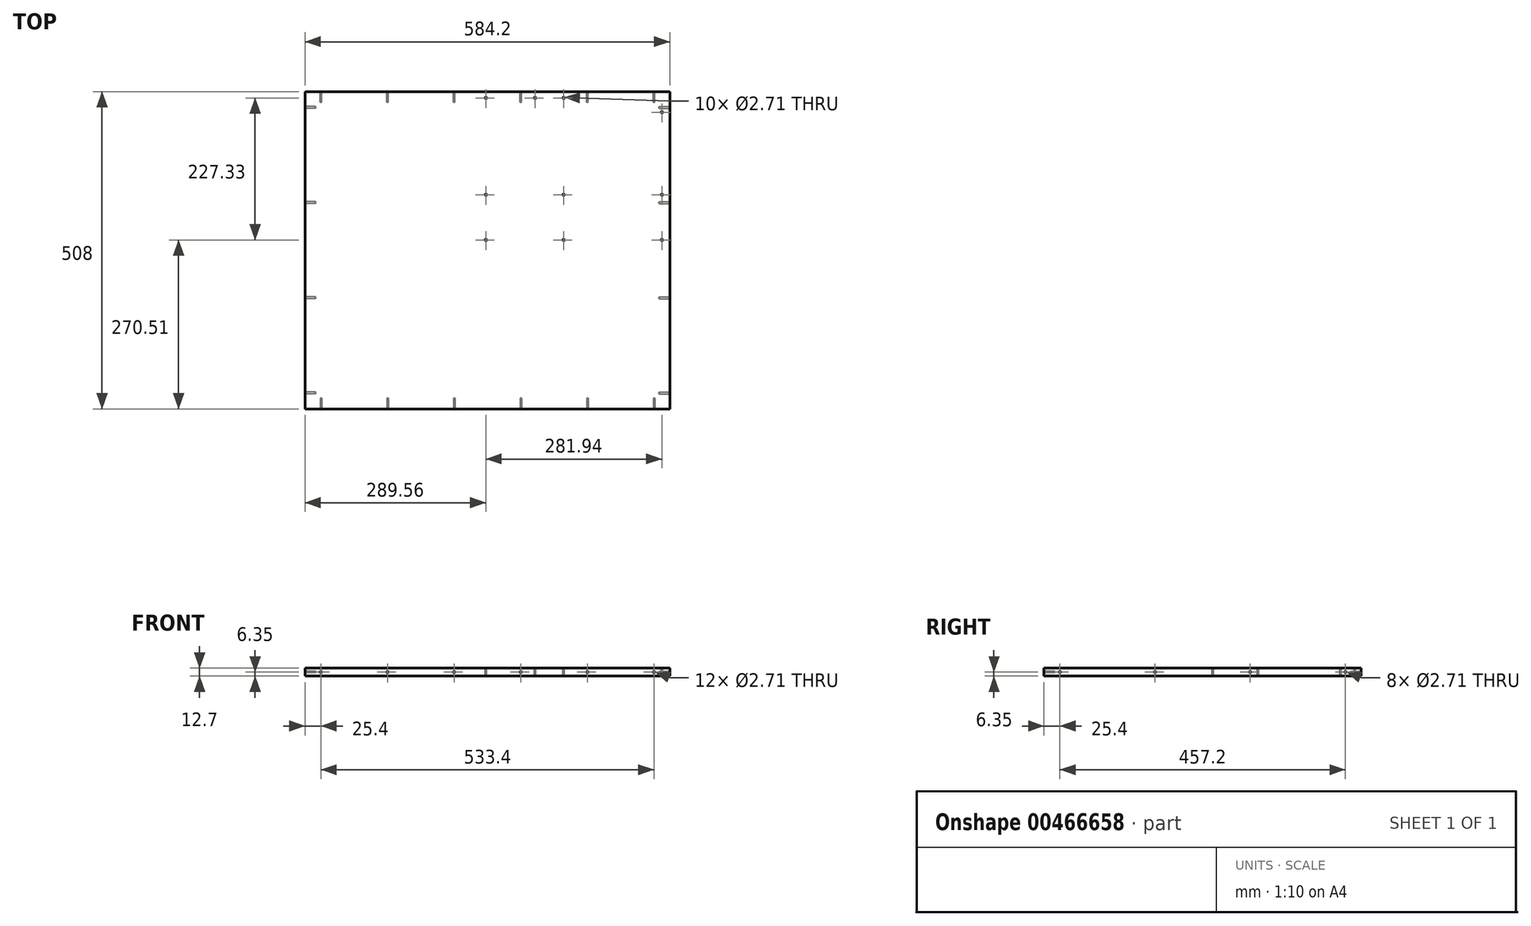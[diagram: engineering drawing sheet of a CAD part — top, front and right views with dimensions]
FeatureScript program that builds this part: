
annotation { "Feature Type Name" : "Feature", "Feature Type Description" : "" }
export const myFeature = defineFeature(function(context is Context, id is Id, definition is map)
    precondition{}
    {
        {
            var Q0;
            Q0=qCreatedBy(makeId("Top.planeOp"),FACE);
            var sketch = newSketch(context, id + "F0", { "sketchPlane" : qUnion([Q0])});
            skLineSegment(sketch, "E0.bottom", {"start": v(0, 0) * mm, "end": v(-584.2, 0) * mm});
            skLineSegment(sketch, "E0.top", {"start": v(0, -508) * mm, "end": v(-584.2, -508) * mm});
            skLineSegment(sketch, "E0.left", {"start": v(0, 0) * mm, "end": v(0, -508) * mm});
            skLineSegment(sketch, "E0.right", {"start": v(-584.2, 0) * mm, "end": v(-584.2, -508) * mm});
            skSolve(sketch);
        }
        {
            var Q0;
            Q0 = qSketchRegion(id + "F0", true);
            extrude(context, id + "F1", {"entities" : qUnion([Q0]), "depth" : 12.7 * mm});
        }
        {
            var Q0;
            Q0=makeQuery(id+"F1.opExtrude","SWEPT_FACE",FACE,{"disambiguationData":[OSD([sQuery(id+"F0.wireOp",EDGE,"E0.left")])]});
            var sketch = newSketch(context, id + "F2", { "sketchPlane" : qUnion([Q0])});
            skPoint(sketch, "E1", {"position": v(-25.4, 6.35) * mm});
            skPoint(sketch, "E2", {"position": v(-722.68, 6.35) * mm});
            skPoint(sketch, "E3", {"position": v(-330.2, 6.35) * mm});
            skPoint(sketch, "E4", {"position": v(-177.8, 6.35) * mm});
            skPoint(sketch, "E5", {"position": v(-482.6, 6.35) * mm});
            skSolve(sketch);
        }
        {
            var Q0;
            Q0=sQuery(id+"F2.wireOp",VERTEX,"E1");
            var Q1;
            Q1=sQuery(id+"F2.wireOp",VERTEX,"E4");
            var Q2;
            Q2=sQuery(id+"F2.wireOp",VERTEX,"E3");
            var Q3;
            Q3=sQuery(id+"F2.wireOp",VERTEX,"E2");
            var Q4;
            Q4=sQuery(id+"F2.wireOp",VERTEX,"E5");
            var Q5;
            Q5=makeQuery(id+"F1.opExtrude","SWEPT_BODY",BODY,{"disambiguationData":[OSD([sQuery(id+"F0.wireOp",EDGE,"E0.bottom"),sQuery(id+"F0.wireOp",EDGE,"E0.top"),sQuery(id+"F0.wireOp",EDGE,"E0.left"),sQuery(id+"F0.wireOp",EDGE,"E0.right")])]});
            hole(context, id + "F3", {"style" : HoleStyle.SIMPLE, "endStyle" : HoleEndStyle.BLIND, "standardTappedOrClearance" : lookupTablePath({ "standard" : "ANSI", "engagement" : "75%", "pitch" : "32 tpi", "size" : "#6", "type" : "Tapped" }), "standardBlindInLast" : lookupTablePath({ "standard" : "ANSI", "engagement" : "75%", "pitch" : "32 tpi", "size" : "#6", "type" : "Tapped" }), "holeDiameter" : 2.7 * mm, "showTappedDepth" : true, "holeDepth" : 16.67 * mm, "isTappedThrough" : true, "tappedDepth" : 12.7 * mm, "tapClearance" : 5, "locations" : qUnion([Q0, Q1, Q2, Q3, Q4]), "scope" : qUnion([Q5]), "majorDiameter" : 3.5 * mm});
        }
        {
            var Q0;
            Q0=makeQuery(id+"F1.opExtrude","SWEPT_FACE",FACE,{"disambiguationData":[OSD([sQuery(id+"F0.wireOp",EDGE,"E0.top")])]});
            var sketch = newSketch(context, id + "F4", { "sketchPlane" : qUnion([Q0])});
            skPoint(sketch, "E6", {"position": v(-25.4, 6.35) * mm});
            skPoint(sketch, "E7.1.0.0", {"position": v(-132.08, 6.35) * mm});
            skPoint(sketch, "E7.2.0.0", {"position": v(-238.76, 6.35) * mm});
            skPoint(sketch, "E7.3.0.0", {"position": v(-345.44, 6.35) * mm});
            skPoint(sketch, "E7.4.0.0", {"position": v(-452.12, 6.35) * mm});
            skLineSegment(sketch, "E7.direction1", {"start": v(-25.4, 6.35) * mm, "end": v(-132.08, 6.35) * mm, "construction": true});
            skPoint(sketch, "E8.0.5.0", {"position": v(-558.8, 6.35) * mm});
            skSolve(sketch);
        }
        {
            var Q0;
            Q0=sQuery(id+"F4.wireOp",VERTEX,"E6");
            var Q1;
            Q1=sQuery(id+"F4.wireOp",VERTEX,"E7.1.0.0");
            var Q2;
            Q2=sQuery(id+"F4.wireOp",VERTEX,"E7.2.0.0");
            var Q3;
            Q3=sQuery(id+"F4.wireOp",VERTEX,"E7.3.0.0");
            var Q4;
            Q4=sQuery(id+"F4.wireOp",VERTEX,"E7.4.0.0");
            var Q5;
            Q5=sQuery(id+"F4.wireOp",VERTEX,"E8.0.5.0");
            var Q6;
            Q6=makeQuery(id+"F1.opExtrude","SWEPT_BODY",BODY,{"disambiguationData":[OSD([sQuery(id+"F0.wireOp",EDGE,"E0.bottom"),sQuery(id+"F0.wireOp",EDGE,"E0.top"),sQuery(id+"F0.wireOp",EDGE,"E0.left"),sQuery(id+"F0.wireOp",EDGE,"E0.right")])]});
            hole(context, id + "F5", {"style" : HoleStyle.SIMPLE, "endStyle" : HoleEndStyle.BLIND, "standardTappedOrClearance" : lookupTablePath({ "standard" : "ANSI", "engagement" : "75%", "pitch" : "32 tpi", "size" : "#6", "type" : "Tapped" }), "standardBlindInLast" : lookupTablePath({ "standard" : "ANSI", "engagement" : "75%", "pitch" : "32 tpi", "size" : "#6", "type" : "Tapped" }), "holeDiameter" : 2.7 * mm, "showTappedDepth" : true, "holeDepth" : 16.66 * mm, "isTappedThrough" : true, "tappedDepth" : 12.7 * mm, "tapClearance" : 5, "locations" : qUnion([Q0, Q1, Q2, Q3, Q4, Q5]), "scope" : qUnion([Q6]), "majorDiameter" : 3.5 * mm});
        }
        {
            var Q0;
            Q0=makeQuery(id+"F1.opExtrude","SWEPT_FACE",FACE,{"disambiguationData":[OSD([sQuery(id+"F0.wireOp",EDGE,"E0.right")])]});
            var sketch = newSketch(context, id + "F6", { "sketchPlane" : qUnion([Q0])});
            skPoint(sketch, "E9", {"position": v(482.6, 6.35) * mm});
            skPoint(sketch, "E10.1.0.0", {"position": v(330.2, 6.35) * mm});
            skPoint(sketch, "E10.2.0.0", {"position": v(177.8, 6.35) * mm});
            skPoint(sketch, "E10.3.0.0", {"position": v(25.4, 6.35) * mm});
            skLineSegment(sketch, "E10.direction1", {"start": v(482.6, 6.35) * mm, "end": v(330.2, 6.35) * mm, "construction": true});
            skSolve(sketch);
        }
        {
            var Q0;
            Q0=sQuery(id+"F6.wireOp",VERTEX,"E9");
            var Q1;
            Q1=sQuery(id+"F6.wireOp",VERTEX,"E10.1.0.0");
            var Q2;
            Q2=sQuery(id+"F6.wireOp",VERTEX,"E10.2.0.0");
            var Q3;
            Q3=sQuery(id+"F6.wireOp",VERTEX,"E10.3.0.0");
            var Q4;
            Q4=makeQuery(id+"F1.opExtrude","SWEPT_BODY",BODY,{"disambiguationData":[OSD([sQuery(id+"F0.wireOp",EDGE,"E0.bottom"),sQuery(id+"F0.wireOp",EDGE,"E0.top"),sQuery(id+"F0.wireOp",EDGE,"E0.left"),sQuery(id+"F0.wireOp",EDGE,"E0.right")])]});
            hole(context, id + "F7", {"style" : HoleStyle.SIMPLE, "endStyle" : HoleEndStyle.BLIND, "standardTappedOrClearance" : lookupTablePath({ "standard" : "ANSI", "engagement" : "75%", "pitch" : "32 tpi", "size" : "#6", "type" : "Tapped" }), "standardBlindInLast" : lookupTablePath({ "standard" : "ANSI", "engagement" : "75%", "pitch" : "32 tpi", "size" : "#6", "type" : "Tapped" }), "holeDiameter" : 2.7 * mm, "showTappedDepth" : true, "holeDepth" : 16.66 * mm, "isTappedThrough" : true, "tappedDepth" : 12.7 * mm, "tapClearance" : 5, "locations" : qUnion([Q0, Q1, Q2, Q3]), "scope" : qUnion([Q4]), "majorDiameter" : 3.5 * mm});
        }
        {
            var Q0;
            Q0=makeQuery(id+"F1.opExtrude","SWEPT_FACE",FACE,{"disambiguationData":[OSD([sQuery(id+"F0.wireOp",EDGE,"E0.bottom")])]});
            var sketch = newSketch(context, id + "F8", { "sketchPlane" : qUnion([Q0])});
            skPoint(sketch, "E11", {"position": v(25.4, 6.35) * mm});
            skPoint(sketch, "E12.1.0.0", {"position": v(132.08, 6.35) * mm});
            skPoint(sketch, "E12.2.0.0", {"position": v(238.76, 6.35) * mm});
            skPoint(sketch, "E12.3.0.0", {"position": v(345.44, 6.35) * mm});
            skPoint(sketch, "E12.4.0.0", {"position": v(452.12, 6.35) * mm});
            skPoint(sketch, "E12.5.0.0", {"position": v(558.8, 6.35) * mm});
            skLineSegment(sketch, "E12.direction1", {"start": v(25.4, 6.35) * mm, "end": v(132.08, 6.35) * mm, "construction": true});
            skSolve(sketch);
        }
        {
            var Q0;
            Q0=sQuery(id+"F8.wireOp",VERTEX,"E11");
            var Q1;
            Q1=sQuery(id+"F8.wireOp",VERTEX,"E12.1.0.0");
            var Q2;
            Q2=sQuery(id+"F8.wireOp",VERTEX,"E12.2.0.0");
            var Q3;
            Q3=sQuery(id+"F8.wireOp",VERTEX,"E12.3.0.0");
            var Q4;
            Q4=sQuery(id+"F8.wireOp",VERTEX,"E12.4.0.0");
            var Q5;
            Q5=sQuery(id+"F8.wireOp",VERTEX,"E12.5.0.0");
            var Q6;
            Q6=makeQuery(id+"F1.opExtrude","SWEPT_BODY",BODY,{"disambiguationData":[OSD([sQuery(id+"F0.wireOp",EDGE,"E0.bottom"),sQuery(id+"F0.wireOp",EDGE,"E0.top"),sQuery(id+"F0.wireOp",EDGE,"E0.left"),sQuery(id+"F0.wireOp",EDGE,"E0.right")])]});
            hole(context, id + "F9", {"style" : HoleStyle.SIMPLE, "endStyle" : HoleEndStyle.BLIND, "standardTappedOrClearance" : lookupTablePath({ "standard" : "ANSI", "engagement" : "75%", "pitch" : "32 tpi", "size" : "#6", "type" : "Tapped" }), "standardBlindInLast" : lookupTablePath({ "standard" : "ANSI", "engagement" : "75%", "pitch" : "32 tpi", "size" : "#6", "type" : "Tapped" }), "holeDiameter" : 2.7 * mm, "showTappedDepth" : true, "holeDepth" : 16.66 * mm, "isTappedThrough" : true, "tappedDepth" : 12.7 * mm, "tapClearance" : 5, "locations" : qUnion([Q0, Q1, Q2, Q3, Q4, Q5]), "scope" : qUnion([Q6]), "majorDiameter" : 3.5 * mm});
        }
        {
            var Q0;
            Q0=makeQuery(id+"F1.opExtrude","CAP_FACE",FACE,{"disambiguationData":[OSD([sQuery(id+"F0.wireOp",EDGE,"E0.bottom"),sQuery(id+"F0.wireOp",EDGE,"E0.top"),sQuery(id+"F0.wireOp",EDGE,"E0.left"),sQuery(id+"F0.wireOp",EDGE,"E0.right")])],"isStart":false});
            var sketch = newSketch(context, id + "F10", { "sketchPlane" : qUnion([Q0])});
            skPoint(sketch, "E13", {"position": v(-12.7, -33.02) * mm});
            skPoint(sketch, "E14", {"position": v(-12.7, -165.1) * mm});
            skPoint(sketch, "E15", {"position": v(-170.18, -10.16) * mm});
            skPoint(sketch, "E16", {"position": v(-215.9, -10.16) * mm});
            skPoint(sketch, "E17", {"position": v(-170.18, -237.5) * mm});
            skPoint(sketch, "E18", {"position": v(-12.7, -237.5) * mm});
            skPoint(sketch, "E19", {"position": v(-170.18, -165.1) * mm});
            skPoint(sketch, "E20", {"position": v(-294.64, -165.1) * mm});
            skPoint(sketch, "E21", {"position": v(-294.64, -237.5) * mm});
            skPoint(sketch, "E22", {"position": v(-294.64, -10.16) * mm});
            skSolve(sketch);
        }
        {
            var Q0;
            Q0=sQuery(id+"F10.wireOp",VERTEX,"E13");
            var Q1;
            Q1=sQuery(id+"F10.wireOp",VERTEX,"E20");
            var Q2;
            Q2=sQuery(id+"F10.wireOp",VERTEX,"E17");
            var Q3;
            Q3=sQuery(id+"F10.wireOp",VERTEX,"E19");
            var Q4;
            Q4=sQuery(id+"F10.wireOp",VERTEX,"E21");
            var Q5;
            Q5=sQuery(id+"F10.wireOp",VERTEX,"E18");
            var Q6;
            Q6=sQuery(id+"F10.wireOp",VERTEX,"E22");
            var Q7;
            Q7=sQuery(id+"F10.wireOp",VERTEX,"E14");
            var Q8;
            Q8=sQuery(id+"F10.wireOp",VERTEX,"E15");
            var Q9;
            Q9=sQuery(id+"F10.wireOp",VERTEX,"E16");
            var Q10;
            Q10=makeQuery(id+"F1.opExtrude","SWEPT_BODY",BODY,{"disambiguationData":[OSD([sQuery(id+"F0.wireOp",EDGE,"E0.bottom"),sQuery(id+"F0.wireOp",EDGE,"E0.top"),sQuery(id+"F0.wireOp",EDGE,"E0.left"),sQuery(id+"F0.wireOp",EDGE,"E0.right")])]});
            hole(context, id + "F11", {"style" : HoleStyle.SIMPLE, "endStyle" : HoleEndStyle.BLIND, "standardTappedOrClearance" : lookupTablePath({ "standard" : "ANSI", "engagement" : "75%", "pitch" : "32 tpi", "size" : "#6", "type" : "Tapped" }), "standardBlindInLast" : lookupTablePath({ "standard" : "ANSI", "engagement" : "75%", "pitch" : "32 tpi", "size" : "#6", "type" : "Tapped" }), "holeDiameter" : 2.7 * mm, "showTappedDepth" : true, "holeDepth" : 10.32 * mm, "isTappedThrough" : true, "tappedDepth" : 6.35 * mm, "tapClearance" : 5, "locations" : qUnion([Q0, Q1, Q2, Q3, Q4, Q5, Q6, Q7, Q8, Q9]), "scope" : qUnion([Q10]), "majorDiameter" : 3.5 * mm});
        }
    });
